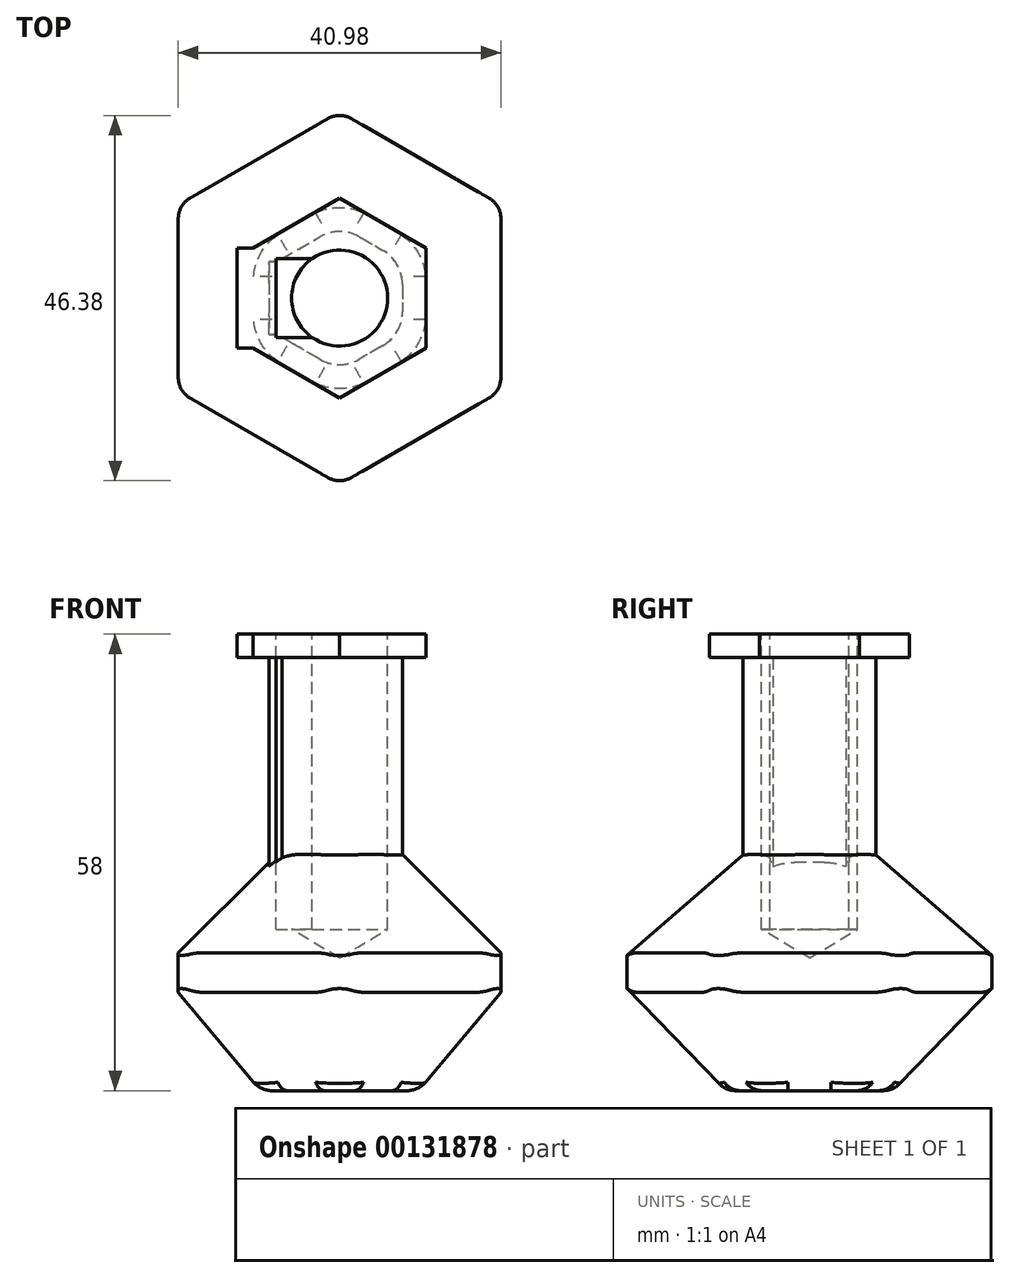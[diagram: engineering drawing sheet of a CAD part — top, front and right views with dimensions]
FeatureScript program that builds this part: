
annotation { "Feature Type Name" : "Feature", "Feature Type Description" : "" }
export const myFeature = defineFeature(function(context is Context, id is Id, definition is map)
    precondition{}
    {
        {
            var Q0;
            Q0=qCreatedBy(makeId("Top.planeOp"),FACE);
            var sketch = newSketch(context, id + "F0", { "sketchPlane" : qUnion([Q0])});
            skCircle(sketch, "E0.cCircle", {"center": v(0, 0) * mm, "radius": 11.55 * mm, "construction": true});
            skLineSegment(sketch, "E0.0", {"start": v(0, 11.55) * mm, "end": v(10, 5.77) * mm});
            skLineSegment(sketch, "E0.1", {"start": v(10, 5.77) * mm, "end": v(10, -5.77) * mm});
            skLineSegment(sketch, "E0.2", {"start": v(10, -5.77) * mm, "end": v(0, -11.55) * mm});
            skLineSegment(sketch, "E0.3", {"start": v(0, -11.55) * mm, "end": v(-10, -5.77) * mm});
            skLineSegment(sketch, "E0.4", {"start": v(-10, -5.77) * mm, "end": v(-10, 5.77) * mm});
            skLineSegment(sketch, "E0.5", {"start": v(-10, 5.77) * mm, "end": v(0, 11.55) * mm});
            skSolve(sketch);
        }
        {
            var Q0;
            Q0 = qSketchRegion(id + "F0", true);
            extrude(context, id + "F1", {"entities" : qUnion([Q0]), "depth" : 12.5 * mm, "hasDraft" : true, "draftAngle" : 40 * degree});
        }
        {
            var Q0;
            Q0=makeQuery(id+"F1.opExtrude","CAP_FACE",FACE,{"disambiguationData":[OSD([sQuery(id+"F0.wireOp",EDGE,"E0.0"),sQuery(id+"F0.wireOp",EDGE,"E0.1"),sQuery(id+"F0.wireOp",EDGE,"E0.2"),sQuery(id+"F0.wireOp",EDGE,"E0.3"),sQuery(id+"F0.wireOp",EDGE,"E0.4"),sQuery(id+"F0.wireOp",EDGE,"E0.5")])],"isStart":false});
            var sketch = newSketch(context, id + "F2", { "sketchPlane" : qUnion([Q0])});
            skLineSegment(sketch, "E1.0", {"start": v(-20.49, 11.83) * mm, "end": v(0, 23.66) * mm});
            skLineSegment(sketch, "E1.1", {"start": v(20.49, 11.83) * mm, "end": v(20.49, -11.83) * mm});
            skLineSegment(sketch, "E1.2", {"start": v(20.49, -11.83) * mm, "end": v(0, -23.66) * mm});
            skLineSegment(sketch, "E1.3", {"start": v(0, 23.66) * mm, "end": v(20.49, 11.83) * mm});
            skLineSegment(sketch, "E1.4", {"start": v(0, -23.66) * mm, "end": v(-20.49, -11.83) * mm});
            skLineSegment(sketch, "E1.5", {"start": v(-20.49, -11.83) * mm, "end": v(-20.49, 11.83) * mm});
            skSolve(sketch);
        }
        {
            var Q0;
            Q0 = qSketchRegion(id + "F2", true);
            extrude(context, id + "F3", {"entities" : qUnion([Q0]), "operationType" : NewBodyOperationType.ADD, "depth" : 5 * mm});
        }
        {
            var Q0;
            Q0=makeQuery(id+"F3.opExtrude","CAP_FACE",FACE,{"disambiguationData":[OSD([sQuery(id+"F2.wireOp",EDGE,"E1.0"),sQuery(id+"F2.wireOp",EDGE,"E1.1"),sQuery(id+"F2.wireOp",EDGE,"E1.2"),sQuery(id+"F2.wireOp",EDGE,"E1.3"),sQuery(id+"F2.wireOp",EDGE,"E1.4"),sQuery(id+"F2.wireOp",EDGE,"E1.5")])],"isStart":false});
            var sketch = newSketch(context, id + "F4", { "sketchPlane" : qUnion([Q0])});
            skSolve(sketch);
        }
        {
            var Q0;
            Q0=makeQuery(id+"F4.imprint","IMPRINT",FACE,{"disambiguationData":[TD([[makeQuery(id+"F4.imprint","IMPRINT",EDGE,{"derivedFrom":makeQuery(id+"F3.opExtrude","CAP_EDGE",EDGE,{"disambiguationData":[OSD([sQuery(id+"F2.wireOp",EDGE,"E1.0")])],"isStart":false})}),-1.0]])]});
            var Q1;
            Q1 = qSketchRegion(id + "F4", true);
            extrude(context, id + "F5", {"entities" : qUnion([Q0, Q1]), "operationType" : NewBodyOperationType.ADD, "depth" : 12.5 * mm, "hasDraft" : true, "draftAngle" : 45 * degree, "draftPullDirection" : true});
        }
        {
            var Q0;
            Q0=makeQuery(id+"F5.opExtrude","CAP_FACE",FACE,{"disambiguationData":[OSD([sQuery(id+"F2.wireOp",EDGE,"E1.0"),sQuery(id+"F2.wireOp",EDGE,"E1.1"),sQuery(id+"F2.wireOp",EDGE,"E1.2"),sQuery(id+"F2.wireOp",EDGE,"E1.3"),sQuery(id+"F2.wireOp",EDGE,"E1.4"),sQuery(id+"F2.wireOp",EDGE,"E1.5")])],"isStart":false});
            var sketch = newSketch(context, id + "F6", { "sketchPlane" : qUnion([Q0])});
            skSolve(sketch);
        }
        {
            var Q0;
            Q0=makeQuery(id+"F6.imprint","IMPRINT",FACE,{"disambiguationData":[TD([[makeQuery(id+"F6.imprint","IMPRINT",EDGE,{"derivedFrom":makeQuery(id+"F5.opExtrude","CAP_EDGE",EDGE,{"disambiguationData":[OSD([sQuery(id+"F2.wireOp",EDGE,"E1.0")])],"isStart":false})}),-1.0]])]});
            extrude(context, id + "F7", {"entities" : qUnion([Q0]), "operationType" : NewBodyOperationType.ADD, "depth" : 25 * mm});
        }
        {
            var Q0;
            Q0=makeQuery(id+"F7.opExtrude","CAP_FACE",FACE,{"disambiguationData":[OSD([sQuery(id+"F2.wireOp",EDGE,"E1.0"),sQuery(id+"F2.wireOp",EDGE,"E1.1"),sQuery(id+"F2.wireOp",EDGE,"E1.2"),sQuery(id+"F2.wireOp",EDGE,"E1.3"),sQuery(id+"F2.wireOp",EDGE,"E1.4"),sQuery(id+"F2.wireOp",EDGE,"E1.5")])],"isStart":false});
            var sketch = newSketch(context, id + "F8", { "sketchPlane" : qUnion([Q0])});
            skLineSegment(sketch, "E2.0", {"start": v(10.99, -6.34) * mm, "end": v(10.99, 6.34) * mm});
            skLineSegment(sketch, "E2.1", {"start": v(0, 12.69) * mm, "end": v(-10.99, 6.34) * mm});
            skLineSegment(sketch, "E2.2", {"start": v(-10.99, 6.34) * mm, "end": v(-10.99, -6.34) * mm});
            skLineSegment(sketch, "E2.3", {"start": v(10.99, 6.34) * mm, "end": v(0, 12.69) * mm});
            skLineSegment(sketch, "E2.4", {"start": v(-10.99, -6.34) * mm, "end": v(0, -12.69) * mm});
            skLineSegment(sketch, "E2.5", {"start": v(0, -12.69) * mm, "end": v(10.99, -6.34) * mm});
            skSolve(sketch);
        }
        {
            var Q0;
            Q0=makeQuery(id+"F8.imprint","IMPRINT",FACE,{"disambiguationData":[TD([[makeQuery(id+"F8.imprint","IMPRINT",EDGE,{"derivedFrom":makeQuery(id+"F7.opExtrude","CAP_EDGE",EDGE,{"disambiguationData":[OSD([sQuery(id+"F2.wireOp",EDGE,"E1.0")])],"isStart":false})}),-1.0]])]});
            var Q1;
            Q1=makeQuery(id+"F8.imprint","IMPRINT",FACE,{"disambiguationData":[TD([[makeQuery(id+"F8.imprint","IMPRINT",EDGE,{"derivedFrom":sQuery(id+"F8.wireOp",EDGE,"E2.0")}),1.0]])]});
            extrude(context, id + "F9", {"entities" : qUnion([Q0, Q1]), "operationType" : NewBodyOperationType.ADD, "depth" : 3 * mm});
        }
        {
            var Q0;
            Q0=makeQuery(id+"F9.opExtrude","CAP_FACE",FACE,{"disambiguationData":[OSD([sQuery(id+"F8.wireOp",EDGE,"E2.0"),sQuery(id+"F8.wireOp",EDGE,"E2.1"),sQuery(id+"F8.wireOp",EDGE,"E2.2"),sQuery(id+"F8.wireOp",EDGE,"E2.3"),sQuery(id+"F8.wireOp",EDGE,"E2.4"),sQuery(id+"F8.wireOp",EDGE,"E2.5")])],"isStart":false});
            var sketch = newSketch(context, id + "F10", { "sketchPlane" : qUnion([Q0])});
            skPoint(sketch, "E3", {"position": v(0, 0) * mm});
            skSolve(sketch);
        }
        {
            var Q0;
            Q0=sQuery(id+"F10.wireOp",VERTEX,"E3");
            var Q1;
            Q1=makeQuery(id+"F1.opExtrude","SWEPT_BODY",BODY,{"disambiguationData":[OSD([sQuery(id+"F0.wireOp",EDGE,"E0.0"),sQuery(id+"F0.wireOp",EDGE,"E0.1"),sQuery(id+"F0.wireOp",EDGE,"E0.2"),sQuery(id+"F0.wireOp",EDGE,"E0.3"),sQuery(id+"F0.wireOp",EDGE,"E0.4"),sQuery(id+"F0.wireOp",EDGE,"E0.5")])]});
            hole(context, id + "F11", {"style" : HoleStyle.SIMPLE, "endStyle" : HoleEndStyle.BLIND, "holeDiameter" : 12.2 * mm, "holeDepth" : 37.5 * mm, "locations" : qUnion([Q0]), "scope" : qUnion([Q1])});
        }
        {
            var Q0;
            Q0=makeQuery(id+"F7.opExtrude","SWEPT_FACE",FACE,{"disambiguationData":[OSD([sQuery(id+"F2.wireOp",EDGE,"E1.5")])]});
            var sketch = newSketch(context, id + "F12", { "sketchPlane" : qUnion([Q0])});
            skPoint(sketch, "E4.oppositeSnap0", {"position": v(4.61, 42.5) * mm});
            skLineSegment(sketch, "E4.bottom", {"start": v(-4.61, 57.58) * mm, "end": v(4.61, 57.58) * mm});
            skLineSegment(sketch, "E4.top", {"start": v(-4.61, 27.58) * mm, "end": v(4.61, 27.58) * mm});
            skLineSegment(sketch, "E4.left", {"start": v(-4.61, 57.58) * mm, "end": v(-4.61, 27.58) * mm});
            skLineSegment(sketch, "E4.right", {"start": v(4.61, 57.58) * mm, "end": v(4.61, 27.58) * mm});
            skSolve(sketch);
        }
        {
            var Q0;
            Q0 = qSketchRegion(id + "F12", true);
            extrude(context, id + "F13", {"entities" : qUnion([Q0]), "operationType" : NewBodyOperationType.ADD, "depth" : 1 * mm});
        }
        {
            var Q0;
            Q0=makeQuery(id+"F9.opExtrude","SWEPT_FACE",FACE,{"disambiguationData":[OSD([sQuery(id+"F8.wireOp",EDGE,"E2.2")])]});
            extrude(context, id + "F14", {"entities" : qUnion([Q0]), "operationType" : NewBodyOperationType.ADD, "depth" : 2 * mm});
        }
        {
            var Q0;
            Q0=makeQuery(id+"F7.opExtrude","SWEPT_EDGE",EDGE,{"disambiguationData":[OSD([sQuery(id+"F2.wireOp",EDGE,"E1.0"),sQuery(id+"F2.wireOp",EDGE,"E1.3")])]});
            var Q1;
            Q1=makeQuery(id+"F7.opExtrude","SWEPT_EDGE",EDGE,{"disambiguationData":[OSD([sQuery(id+"F2.wireOp",EDGE,"E1.1"),sQuery(id+"F2.wireOp",EDGE,"E1.3")])]});
            var Q2;
            Q2=makeQuery(id+"F7.opExtrude","SWEPT_EDGE",EDGE,{"disambiguationData":[OSD([sQuery(id+"F2.wireOp",EDGE,"E1.1"),sQuery(id+"F2.wireOp",EDGE,"E1.2")])]});
            var Q3;
            Q3=makeQuery(id+"F7.opExtrude","SWEPT_EDGE",EDGE,{"disambiguationData":[OSD([sQuery(id+"F2.wireOp",EDGE,"E1.2"),sQuery(id+"F2.wireOp",EDGE,"E1.4")])]});
            fillet(context, id + "F15", {"entities" : qUnion([Q0, Q1, Q2, Q3]), "radius" : 5 * mm, "tangentPropagation" : true, "allowEdgeOverflow" : false});
        }
        {
            var Q0;
            Q0=makeQuery(id+"F5.opExtrude","SWEPT_EDGE",EDGE,{"disambiguationData":[OSD([sQuery(id+"F2.wireOp",EDGE,"E1.1"),sQuery(id+"F2.wireOp",EDGE,"E1.3")])]});
            var Q1;
            Q1=makeQuery(id+"F5.opExtrude","SWEPT_EDGE",EDGE,{"disambiguationData":[OSD([sQuery(id+"F2.wireOp",EDGE,"E1.0"),sQuery(id+"F2.wireOp",EDGE,"E1.3")])]});
            var Q2;
            Q2=makeQuery(id+"F5.opExtrude","SWEPT_EDGE",EDGE,{"disambiguationData":[OSD([sQuery(id+"F2.wireOp",EDGE,"E1.0"),sQuery(id+"F2.wireOp",EDGE,"E1.5")])]});
            var Q3;
            Q3=makeQuery(id+"F5.opExtrude","SWEPT_EDGE",EDGE,{"disambiguationData":[OSD([sQuery(id+"F2.wireOp",EDGE,"E1.4"),sQuery(id+"F2.wireOp",EDGE,"E1.5")])]});
            var Q4;
            Q4=makeQuery(id+"F5.opExtrude","SWEPT_EDGE",EDGE,{"disambiguationData":[OSD([sQuery(id+"F2.wireOp",EDGE,"E1.2"),sQuery(id+"F2.wireOp",EDGE,"E1.4")])]});
            var Q5;
            Q5=makeQuery(id+"F5.opExtrude","SWEPT_EDGE",EDGE,{"disambiguationData":[OSD([sQuery(id+"F2.wireOp",EDGE,"E1.1"),sQuery(id+"F2.wireOp",EDGE,"E1.2")])]});
            var Q6;
            Q6=makeQuery(id+"F1.opExtrude","SWEPT_EDGE",EDGE,{"disambiguationData":[OSD([sQuery(id+"F0.wireOp",EDGE,"E0.2"),sQuery(id+"F0.wireOp",EDGE,"E0.3")])]});
            var Q7;
            Q7=makeQuery(id+"F1.opExtrude","SWEPT_EDGE",EDGE,{"disambiguationData":[OSD([sQuery(id+"F0.wireOp",EDGE,"E0.1"),sQuery(id+"F0.wireOp",EDGE,"E0.2")])]});
            var Q8;
            Q8=makeQuery(id+"F1.opExtrude","SWEPT_EDGE",EDGE,{"disambiguationData":[OSD([sQuery(id+"F0.wireOp",EDGE,"E0.0"),sQuery(id+"F0.wireOp",EDGE,"E0.1")])]});
            var Q9;
            Q9=makeQuery(id+"F1.opExtrude","SWEPT_EDGE",EDGE,{"disambiguationData":[OSD([sQuery(id+"F0.wireOp",EDGE,"E0.0"),sQuery(id+"F0.wireOp",EDGE,"E0.5")])]});
            var Q10;
            Q10=makeQuery(id+"F1.opExtrude","SWEPT_EDGE",EDGE,{"disambiguationData":[OSD([sQuery(id+"F0.wireOp",EDGE,"E0.4"),sQuery(id+"F0.wireOp",EDGE,"E0.5")])]});
            var Q11;
            Q11=makeQuery(id+"F1.opExtrude","SWEPT_EDGE",EDGE,{"disambiguationData":[OSD([sQuery(id+"F0.wireOp",EDGE,"E0.3"),sQuery(id+"F0.wireOp",EDGE,"E0.4")])]});
            fillet(context, id + "F16", {"entities" : qUnion([Q0, Q1, Q2, Q3, Q4, Q5, Q6, Q7, Q8, Q9, Q10, Q11]), "radius" : 8 * mm, "tangentPropagation" : true, "allowEdgeOverflow" : false});
        }
        {
            var Q0;
            Q0=makeQuery(id+"F3.opExtrude","SWEPT_EDGE",EDGE,{"disambiguationData":[OSD([sQuery(id+"F2.wireOp",EDGE,"E1.0"),sQuery(id+"F2.wireOp",EDGE,"E1.3")])]});
            var Q1;
            Q1=makeQuery(id+"F3.opExtrude","SWEPT_EDGE",EDGE,{"disambiguationData":[OSD([sQuery(id+"F2.wireOp",EDGE,"E1.0"),sQuery(id+"F2.wireOp",EDGE,"E1.5")])]});
            var Q2;
            Q2=makeQuery(id+"F3.opExtrude","SWEPT_EDGE",EDGE,{"disambiguationData":[OSD([sQuery(id+"F2.wireOp",EDGE,"E1.4"),sQuery(id+"F2.wireOp",EDGE,"E1.5")])]});
            var Q3;
            Q3=makeQuery(id+"F3.opExtrude","SWEPT_EDGE",EDGE,{"disambiguationData":[OSD([sQuery(id+"F2.wireOp",EDGE,"E1.2"),sQuery(id+"F2.wireOp",EDGE,"E1.4")])]});
            var Q4;
            Q4=makeQuery(id+"F3.opExtrude","SWEPT_EDGE",EDGE,{"disambiguationData":[OSD([sQuery(id+"F2.wireOp",EDGE,"E1.1"),sQuery(id+"F2.wireOp",EDGE,"E1.2")])]});
            var Q5;
            Q5=makeQuery(id+"F3.opExtrude","SWEPT_EDGE",EDGE,{"disambiguationData":[OSD([sQuery(id+"F2.wireOp",EDGE,"E1.1"),sQuery(id+"F2.wireOp",EDGE,"E1.3")])]});
            var Q6;
            Q6=makeQuery(id+"F1.opExtrude","CAP_FACE",FACE,{"disambiguationData":[OSD([sQuery(id+"F0.wireOp",EDGE,"E0.0"),sQuery(id+"F0.wireOp",EDGE,"E0.1"),sQuery(id+"F0.wireOp",EDGE,"E0.2"),sQuery(id+"F0.wireOp",EDGE,"E0.3"),sQuery(id+"F0.wireOp",EDGE,"E0.4"),sQuery(id+"F0.wireOp",EDGE,"E0.5")])],"isStart":true});
            fillet(context, id + "F17", {"entities" : qUnion([Q0, Q1, Q2, Q3, Q4, Q5, Q6]), "radius" : 3 * mm, "tangentPropagation" : true, "allowEdgeOverflow" : false});
        }
        {
            var Q0;
            {var subQ0=sQuery(id+"F8.wireOp",EDGE,"E2.2");Q0=makeQuery(id+"F14.boolean.opBoolean","MERGE",FACE,{"derivedFrom":[makeQuery(id+"F9.opExtrude","CAP_FACE",FACE,{"disambiguationData":[OSD([sQuery(id+"F8.wireOp",EDGE,"E2.0"),sQuery(id+"F8.wireOp",EDGE,"E2.1"),subQ0,sQuery(id+"F8.wireOp",EDGE,"E2.3"),sQuery(id+"F8.wireOp",EDGE,"E2.4"),sQuery(id+"F8.wireOp",EDGE,"E2.5")])],"isStart":false}),makeQuery(id+"F14.opExtrude","SWEPT_FACE",FACE,{"disambiguationData":[OSD([subQ0]),TDD([makeQuery(id+"F9.opExtrude","CAP_EDGE",EDGE,{"disambiguationData":[OSD([subQ0])],"isStart":false})])]})]});}
            var sketch = newSketch(context, id + "F18", { "sketchPlane" : qUnion([Q0])});
            skLineSegment(sketch, "E5.bottom", {"start": v(-8.1, 5) * mm, "end": v(-3.1, 5) * mm});
            skLineSegment(sketch, "E5.top", {"start": v(-8.1, -5) * mm, "end": v(-3.1, -5) * mm});
            skLineSegment(sketch, "E5.left", {"start": v(-8.1, 5) * mm, "end": v(-8.1, -5) * mm});
            skLineSegment(sketch, "E5.right", {"start": v(-3.1, 5) * mm, "end": v(-3.1, -5) * mm});
            skPoint(sketch, "E5.middle", {"position": v(-6.1, 0) * mm});
            skSolve(sketch);
        }
        {
            var Q0;
            Q0 = qSketchRegion(id + "F18", true);
            extrude(context, id + "F19", {"entities" : qUnion([Q0]), "operationType" : NewBodyOperationType.REMOVE, "oppositeDirection" : true, "depth" : 37.5 * mm});
        }
    });
